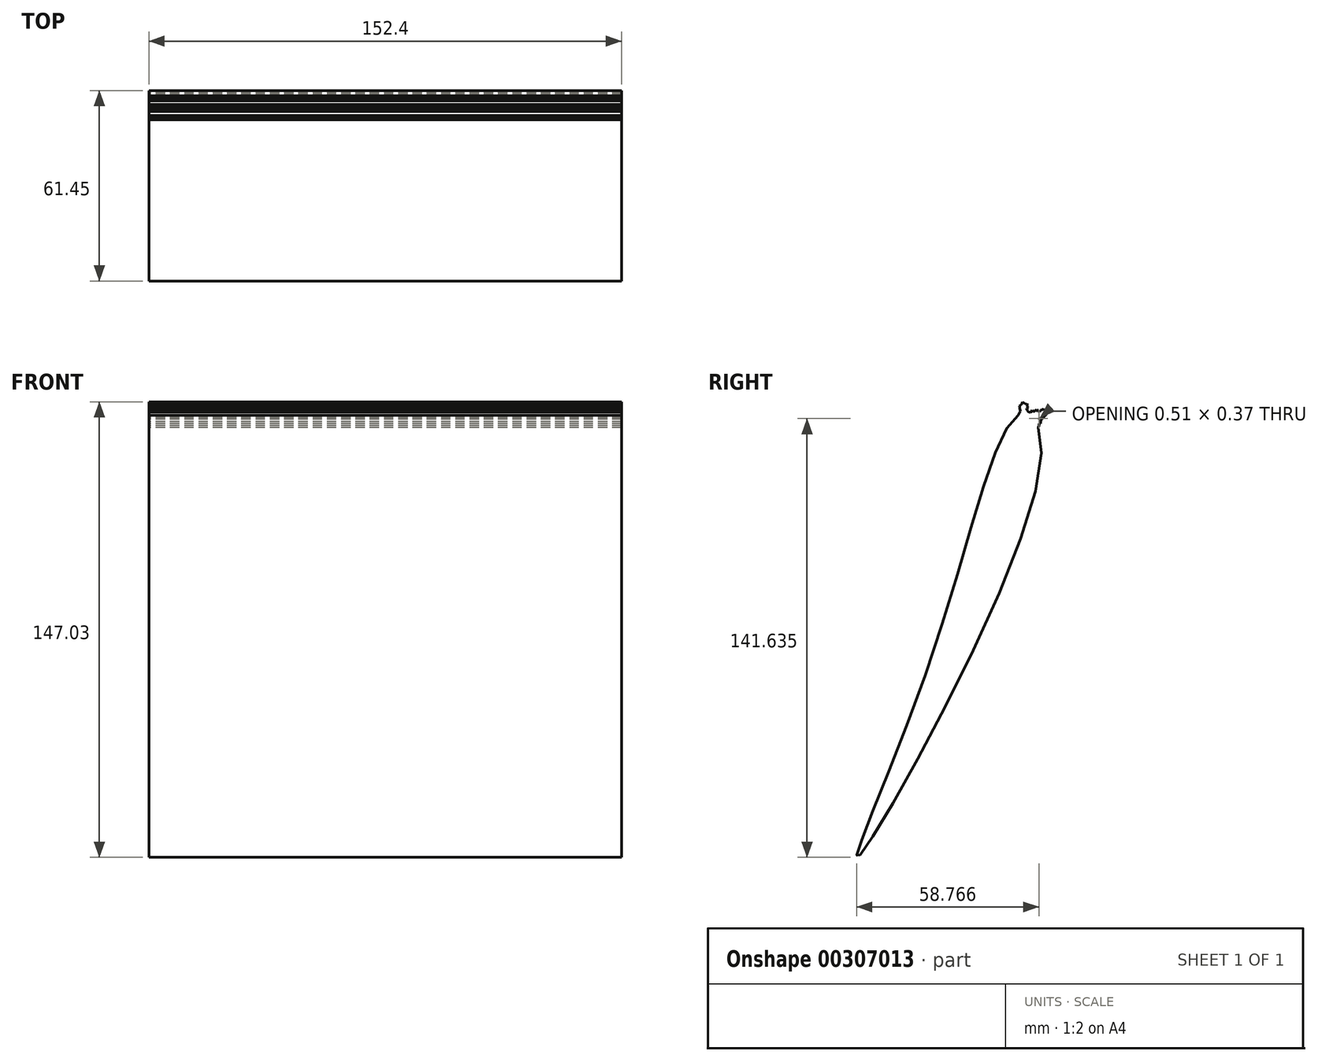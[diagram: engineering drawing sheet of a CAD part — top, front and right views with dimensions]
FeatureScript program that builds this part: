
annotation { "Feature Type Name" : "Feature", "Feature Type Description" : "" }
export const myFeature = defineFeature(function(context is Context, id is Id, definition is map)
    precondition{}
    {
        {
            var Q0;
            Q0=qCreatedBy(makeId("Right.planeOp"),FACE);
            var sketch = newSketch(context, id + "F0", { "sketchPlane" : qUnion([Q0])});
            skFitSpline(sketch, "E0", {"points": [v(49.89, 66.18) * mm, v(56.5, 49.9) * mm, v(-2.03, -76.46) * mm, v(21.12, -12.85) * mm, v(49.89, 66.18) * mm]});
            skLineSegment(sketch, "E1", {"start": v(53.87, 65.13) * mm, "end": v(56.93, 67.06) * mm});
            skLineSegment(sketch, "E2", {"start": v(56.93, 67.06) * mm, "end": v(57.7, 66.01) * mm});
            skLineSegment(sketch, "E3", {"start": v(57.7, 66.01) * mm, "end": v(54.8, 63.9) * mm});
            skLineSegment(sketch, "E4", {"start": v(54.8, 63.9) * mm, "end": v(53.87, 65.13) * mm});
            skLineSegment(sketch, "E5", {"start": v(56.93, 67.06) * mm, "end": v(57.7, 67.62) * mm});
            skPoint(sketch, "E5.endSnap0", {"position": v(57.31, 66.54) * mm});
            skLineSegment(sketch, "E6", {"start": v(57.7, 67.62) * mm, "end": v(58.4, 66.53) * mm});
            skLineSegment(sketch, "E7", {"start": v(58.4, 66.53) * mm, "end": v(57.7, 66.01) * mm});
            skLineSegment(sketch, "E8", {"start": v(51.68, 66.38) * mm, "end": v(51.55, 69.02) * mm});
            skLineSegment(sketch, "E9", {"start": v(51.55, 69.02) * mm, "end": v(50.25, 68.95) * mm});
            skLineSegment(sketch, "E10", {"start": v(50.25, 68.95) * mm, "end": v(50.38, 66.34) * mm});
            skLineSegment(sketch, "E11", {"start": v(50.38, 66.34) * mm, "end": v(51.68, 66.38) * mm});
            skLineSegment(sketch, "E12", {"start": v(55.24, 63.24) * mm, "end": v(55.73, 64.59) * mm});
            skLineSegment(sketch, "E13", {"start": v(55.73, 64.59) * mm, "end": v(56.24, 64.96) * mm});
            skLineSegment(sketch, "E14", {"start": v(56.24, 64.96) * mm, "end": v(56.15, 64.71) * mm});
            skPoint(sketch, "E14.endSnap0", {"position": v(55.99, 64.77) * mm});
            skLineSegment(sketch, "E15", {"start": v(56.15, 64.71) * mm, "end": v(55.73, 64.59) * mm});
            skLineSegment(sketch, "E16", {"start": v(55.48, 63.92) * mm, "end": v(56.31, 64.52) * mm});
            skLineSegment(sketch, "E17", {"start": v(56.31, 64.52) * mm, "end": v(56.56, 65.19) * mm});
            skLineSegment(sketch, "E18", {"start": v(56.56, 65.19) * mm, "end": v(56.89, 64.73) * mm});
            skLineSegment(sketch, "E19", {"start": v(56.89, 64.73) * mm, "end": v(56.31, 64.52) * mm});
            skLineSegment(sketch, "E20", {"start": v(57.3, 65.72) * mm, "end": v(58.09, 65.43) * mm});
            skLineSegment(sketch, "E21", {"start": v(58.09, 65.43) * mm, "end": v(57.7, 66.01) * mm});
            skLineSegment(sketch, "E22", {"start": v(58.4, 66.53) * mm, "end": v(58.23, 65.82) * mm});
            skLineSegment(sketch, "E23", {"start": v(58.23, 65.82) * mm, "end": v(57.4, 65.22) * mm});
            skLineSegment(sketch, "E24", {"start": v(57.4, 65.22) * mm, "end": v(56.56, 65.19) * mm});
            skLineSegment(sketch, "E25", {"start": v(57.4, 65.22) * mm, "end": v(57.3, 64.92) * mm});
            skLineSegment(sketch, "E26", {"start": v(57.3, 64.92) * mm, "end": v(56.89, 64.73) * mm});
            skLineSegment(sketch, "E27", {"start": v(58.23, 65.82) * mm, "end": v(57.7, 66.01) * mm});
            skLineSegment(sketch, "E28", {"start": v(56.89, 64.73) * mm, "end": v(56.55, 63.81) * mm});
            skLineSegment(sketch, "E29", {"start": v(56.55, 63.81) * mm, "end": v(55.48, 63.92) * mm});
            skLineSegment(sketch, "E30", {"start": v(58.4, 66.53) * mm, "end": v(58.67, 67.27) * mm});
            skLineSegment(sketch, "E31", {"start": v(58.67, 67.27) * mm, "end": v(58.16, 66.9) * mm});
            skLineSegment(sketch, "E32", {"start": v(58.16, 66.9) * mm, "end": v(58.67, 67.27) * mm});
            skLineSegment(sketch, "E33", {"start": v(58.67, 67.27) * mm, "end": v(57.7, 67.62) * mm});
            skLineSegment(sketch, "E34", {"start": v(57.7, 67.62) * mm, "end": v(56.94, 67.9) * mm});
            skLineSegment(sketch, "E35", {"start": v(56.94, 67.9) * mm, "end": v(56.66, 67.16) * mm});
            skLineSegment(sketch, "E36", {"start": v(56.66, 67.16) * mm, "end": v(55.66, 67.14) * mm});
            skLineSegment(sketch, "E37", {"start": v(55.66, 67.14) * mm, "end": v(55.28, 67.66) * mm});
            skLineSegment(sketch, "E38", {"start": v(55.28, 67.66) * mm, "end": v(54.89, 66.6) * mm});
            skLineSegment(sketch, "E39", {"start": v(54.89, 66.6) * mm, "end": v(54.74, 66.19) * mm});
            skLineSegment(sketch, "E40", {"start": v(54.74, 66.19) * mm, "end": v(54, 66.27) * mm});
            skLineSegment(sketch, "E41", {"start": v(54, 66.27) * mm, "end": v(53.7, 65.43) * mm});
            skLineSegment(sketch, "E42", {"start": v(53.7, 65.43) * mm, "end": v(53.87, 65.13) * mm});
            skLineSegment(sketch, "E43", {"start": v(55.28, 67.66) * mm, "end": v(54.17, 66.86) * mm});
            skLineSegment(sketch, "E44", {"start": v(54.17, 66.86) * mm, "end": v(53.74, 67.45) * mm});
            skLineSegment(sketch, "E45", {"start": v(53.74, 67.45) * mm, "end": v(53.22, 66.74) * mm});
            skLineSegment(sketch, "E46", {"start": v(53.22, 66.74) * mm, "end": v(52.55, 66.99) * mm});
            skLineSegment(sketch, "E47", {"start": v(52.55, 66.99) * mm, "end": v(51.9, 66.51) * mm});
            skLineSegment(sketch, "E48", {"start": v(52.55, 66.99) * mm, "end": v(52.09, 67.62) * mm});
            skLineSegment(sketch, "E49", {"start": v(52.09, 67.62) * mm, "end": v(51.67, 67.3) * mm});
            skLineSegment(sketch, "E50", {"start": v(51.67, 67.3) * mm, "end": v(51.96, 68.1) * mm});
            skLineSegment(sketch, "E51", {"start": v(51.96, 68.1) * mm, "end": v(51.58, 68.62) * mm});
            skLineSegment(sketch, "E52", {"start": v(51.58, 68.62) * mm, "end": v(51.55, 69.02) * mm});
            skLineSegment(sketch, "E53", {"start": v(51.96, 68.1) * mm, "end": v(52.2, 68.78) * mm});
            skLineSegment(sketch, "E54", {"start": v(52.2, 68.78) * mm, "end": v(51.58, 68.62) * mm});
            skLineSegment(sketch, "E55", {"start": v(52.2, 68.78) * mm, "end": v(52.59, 68.26) * mm});
            skLineSegment(sketch, "E56", {"start": v(52.59, 68.26) * mm, "end": v(51.96, 68.1) * mm});
            skLineSegment(sketch, "E57", {"start": v(52.2, 68.78) * mm, "end": v(52.16, 69.64) * mm});
            skLineSegment(sketch, "E58", {"start": v(52.16, 69.64) * mm, "end": v(51.55, 69.02) * mm});
            skLineSegment(sketch, "E59", {"start": v(51.55, 69.02) * mm, "end": v(51.13, 69.6) * mm});
            skPoint(sketch, "E59.endSnap0", {"position": v(50.9, 68.99) * mm});
            skLineSegment(sketch, "E60", {"start": v(51.13, 69.6) * mm, "end": v(50.25, 68.95) * mm});
            skLineSegment(sketch, "E61", {"start": v(50.25, 68.95) * mm, "end": v(50.7, 70.17) * mm});
            skLineSegment(sketch, "E62", {"start": v(50.7, 70.17) * mm, "end": v(51.86, 69.33) * mm});
            skLineSegment(sketch, "E63", {"start": v(51.86, 69.33) * mm, "end": v(52.16, 69.64) * mm});
            skLineSegment(sketch, "E64", {"start": v(50.43, 69.43) * mm, "end": v(49.72, 68.92) * mm});
            skLineSegment(sketch, "E65", {"start": v(49.72, 68.92) * mm, "end": v(50.34, 67.45) * mm});
            skLineSegment(sketch, "E66", {"start": v(50.34, 67.45) * mm, "end": v(49.8, 68) * mm});
            skLineSegment(sketch, "E67", {"start": v(49.8, 68) * mm, "end": v(49.77, 68.46) * mm});
            skLineSegment(sketch, "E68", {"start": v(49.77, 68.46) * mm, "end": v(49.72, 68.92) * mm});
            skLineSegment(sketch, "E69", {"start": v(50.38, 66.34) * mm, "end": v(49.89, 66.18) * mm});
            skLineSegment(sketch, "E70", {"start": v(49.89, 66.18) * mm, "end": v(49.85, 66.87) * mm});
            skLineSegment(sketch, "E71", {"start": v(49.85, 66.87) * mm, "end": v(50.39, 67.35) * mm});
            skLineSegment(sketch, "E72", {"start": v(50.39, 67.35) * mm, "end": v(49.8, 68) * mm});
            skLineSegment(sketch, "E73", {"start": v(49.8, 68) * mm, "end": v(50.12, 67.1) * mm});
            skLineSegment(sketch, "E74", {"start": v(56.55, 63.81) * mm, "end": v(56.49, 63.12) * mm});
            skLineSegment(sketch, "E75", {"start": v(56.49, 63.12) * mm, "end": v(55.96, 63.1) * mm});
            skLineSegment(sketch, "E76", {"start": v(55.96, 63.1) * mm, "end": v(55.97, 62.47) * mm});
            skLineSegment(sketch, "E77", {"start": v(55.97, 62.47) * mm, "end": v(55.74, 61.85) * mm});
            skLineSegment(sketch, "E78", {"start": v(55.74, 61.85) * mm, "end": v(55.24, 63.24) * mm});
            skLineSegment(sketch, "E79", {"start": v(49.85, 66.87) * mm, "end": v(49.24, 65.86) * mm});
            skLineSegment(sketch, "E80", {"start": v(49.24, 65.86) * mm, "end": v(49.89, 66.18) * mm});
            skLineSegment(sketch, "E81", {"start": v(51.96, 68.1) * mm, "end": v(52.09, 67.62) * mm});
            skLineSegment(sketch, "E82.0", {"start": v(49.85, 66.87) * mm, "end": v(56.31, 64.52) * mm, "construction": true});
            skLineSegment(sketch, "E83.0", {"start": v(49.77, 68.46) * mm, "end": v(58.09, 65.43) * mm, "construction": true});
            skLineSegment(sketch, "E84.0", {"start": v(49.8, 68) * mm, "end": v(52.55, 66.99) * mm, "construction": true});
            skLineSegment(sketch, "E85.0", {"start": v(50.34, 67.45) * mm, "end": v(57.3, 64.92) * mm, "construction": true});
            skLineSegment(sketch, "E86.0", {"start": v(49.72, 68.92) * mm, "end": v(58.23, 65.82) * mm, "construction": true});
            skLineSegment(sketch, "E87.0", {"start": v(50.7, 70.17) * mm, "end": v(58.67, 67.27) * mm, "construction": true});
            skLineSegment(sketch, "E88.0", {"start": v(50.43, 69.43) * mm, "end": v(58.4, 66.53) * mm, "construction": true});
            skLineSegment(sketch, "E89.0", {"start": v(51.58, 68.62) * mm, "end": v(57.31, 66.54) * mm, "construction": true});
            skLineSegment(sketch, "E90.0", {"start": v(55.99, 64.77) * mm, "end": v(56.15, 64.71) * mm, "construction": true});
            skLineSegment(sketch, "E91.0", {"start": v(54.17, 66.86) * mm, "end": v(54.89, 66.6) * mm, "construction": true});
            skLineSegment(sketch, "E92.0", {"start": v(54.74, 66.19) * mm, "end": v(57.4, 65.22) * mm, "construction": true});
            skLineSegment(sketch, "E93.0", {"start": v(50.34, 67.45) * mm, "end": v(51.13, 69.6) * mm, "construction": true});
            skLineSegment(sketch, "E94.0", {"start": v(57.4, 65.22) * mm, "end": v(57.7, 66.01) * mm, "construction": true});
            skLineSegment(sketch, "E95.0", {"start": v(50.25, 68.95) * mm, "end": v(50.43, 69.43) * mm, "construction": true});
            skLineSegment(sketch, "E96.0", {"start": v(57.31, 66.54) * mm, "end": v(57.7, 67.62) * mm, "construction": true});
            skLineSegment(sketch, "E97.0", {"start": v(55.48, 63.92) * mm, "end": v(56.94, 67.9) * mm, "construction": true});
            skLineSegment(sketch, "E98.0", {"start": v(58.09, 65.43) * mm, "end": v(58.23, 65.82) * mm, "construction": true});
            skSolve(sketch);
        }
        {
            var Q0;
            Q0=qSketchRegion(id+"F0",true);
            var Q1;
            Q1=makeQuery(id+"F0.imprint","IMPRINT",FACE,{"disambiguationData":[TD([[makeQuery(id+"F0.imprint","IMPRINT",EDGE,{"derivedFrom":sQuery(id+"F0.wireOp",EDGE,"E1")}),1.0]])]});
            var Q2;
            {var subQ3=sQuery(id+"F0.wireOp",EDGE,"E1");Q2=makeQuery(id+"F0.imprint","IMPRINT",FACE,{"disambiguationData":[TD([[makeQuery(id+"F0.imprint","IMPRINT",EDGE,{"derivedFrom":subQ3}),-1.0]])]});}
            var Q3;
            {var subQ0=sQuery(id+"F0.wireOp",EDGE,"E29");Q3=makeQuery(id+"F0.imprint","IMPRINT",FACE,{"disambiguationData":[TD([[makeQuery(id+"F0.imprint","IMPRINT",EDGE,{"derivedFrom":subQ0}),1.0]])]});}
            var Q4;
            {var subQ0=sQuery(id+"F0.wireOp",EDGE,"E78");var subQ1=sQuery(id+"F0.wireOp",EDGE,"E12");var subQ2=makeQuery(id+"F0.imprint","INTERSECT",VERTEX,{"derivedFrom":[subQ1,subQ0]});Q4=makeQuery(id+"F0.imprint","IMPRINT",FACE,{"disambiguationData":[TD([[makeQuery(id+"F0.imprint","IMPRINT",EDGE,{"disambiguationData":[TD([[subQ2,1.0]])],"derivedFrom":subQ0}),1.0]])]});}
            var Q5;
            {var subQ2=sQuery(id+"F0.wireOp",EDGE,"E8");Q5=makeQuery(id+"F0.imprint","IMPRINT",FACE,{"disambiguationData":[TD([[makeQuery(id+"F0.imprint","IMPRINT",EDGE,{"derivedFrom":subQ2}),-1.0]])]});}
            var Q6;
            {var subQ0=sQuery(id+"F0.wireOp",EDGE,"E11");Q6=makeQuery(id+"F0.imprint","IMPRINT",FACE,{"disambiguationData":[TD([[makeQuery(id+"F0.imprint","IMPRINT",EDGE,{"derivedFrom":subQ0}),1.0]])]});}
            var Q7;
            {var subQ0=sQuery(id+"F0.wireOp",EDGE,"E4");Q7=makeQuery(id+"F0.imprint","IMPRINT",FACE,{"disambiguationData":[TD([[makeQuery(id+"F0.imprint","IMPRINT",EDGE,{"derivedFrom":subQ0}),-1.0]])]});}
            var Q8;
            {var subQ0=sQuery(id+"F0.wireOp",EDGE,"E78");var subQ1=sQuery(id+"F0.wireOp",EDGE,"E0");var subQ3=makeQuery(id+"F0.imprint","INTERSECT",VERTEX,{"derivedFrom":[subQ1,subQ0]});Q8=makeQuery(id+"F0.imprint","IMPRINT",FACE,{"disambiguationData":[TD([[makeQuery(id+"F0.imprint","IMPRINT",EDGE,{"disambiguationData":[TD([[subQ3,-1.0]])],"derivedFrom":subQ1}),-1.0]])]});}
            var Q9;
            {var subQ6=sQuery(id+"F0.wireOp",EDGE,"E8");Q9=makeQuery(id+"F0.imprint","IMPRINT",FACE,{"disambiguationData":[TD([[makeQuery(id+"F0.imprint","IMPRINT",EDGE,{"derivedFrom":subQ6}),1.0]])]});}
            var Q10;
            Q10=makeQuery(id+"F0.imprint","IMPRINT",FACE,{"disambiguationData":[TD([[makeQuery(id+"F0.imprint","IMPRINT",EDGE,{"derivedFrom":sQuery(id+"F0.wireOp",EDGE,"E58")}),-1.0]])]});
            var Q11;
            {var subQ0=sQuery(id+"F0.wireOp",EDGE,"E69");Q11=makeQuery(id+"F0.imprint","IMPRINT",FACE,{"disambiguationData":[TD([[makeQuery(id+"F0.imprint","IMPRINT",EDGE,{"derivedFrom":subQ0}),-1.0]])]});}
            var Q12;
            {var subQ1=sQuery(id+"F0.wireOp",EDGE,"E70");Q12=makeQuery(id+"F0.imprint","IMPRINT",FACE,{"disambiguationData":[TD([[makeQuery(id+"F0.imprint","IMPRINT",EDGE,{"derivedFrom":subQ1}),1.0]])]});}
            var Q13;
            {var subQ0=sQuery(id+"F0.wireOp",EDGE,"E80");Q13=makeQuery(id+"F0.imprint","IMPRINT",FACE,{"disambiguationData":[TD([[makeQuery(id+"F0.imprint","IMPRINT",EDGE,{"derivedFrom":subQ0}),1.0]])]});}
            var Q14;
            {var subQ5=sQuery(id+"F0.wireOp",EDGE,"E64");Q14=makeQuery(id+"F0.imprint","IMPRINT",FACE,{"disambiguationData":[TD([[makeQuery(id+"F0.imprint","IMPRINT",EDGE,{"derivedFrom":subQ5}),1.0]])]});}
            var Q15;
            {var subQ1=sQuery(id+"F0.wireOp",EDGE,"E70");Q15=makeQuery(id+"F0.imprint","IMPRINT",FACE,{"disambiguationData":[TD([[makeQuery(id+"F0.imprint","IMPRINT",EDGE,{"derivedFrom":subQ1}),-1.0]])]});}
            var Q16;
            {var subQ0=sQuery(id+"F0.wireOp",EDGE,"E67");Q16=makeQuery(id+"F0.imprint","IMPRINT",FACE,{"disambiguationData":[TD([[makeQuery(id+"F0.imprint","IMPRINT",EDGE,{"derivedFrom":subQ0}),-1.0]])]});}
            var Q17;
            {var subQ0=sQuery(id+"F0.wireOp",EDGE,"E72");var subQ1=sQuery(id+"F0.wireOp",EDGE,"E10");var subQ2=makeQuery(id+"F0.imprint","INTERSECT",VERTEX,{"derivedFrom":[subQ1,subQ0]});Q17=makeQuery(id+"F0.imprint","IMPRINT",FACE,{"disambiguationData":[TD([[makeQuery(id+"F0.imprint","IMPRINT",EDGE,{"disambiguationData":[TD([[subQ2,-1.0]])],"derivedFrom":subQ1}),1.0]])]});}
            var Q18;
            Q18=makeQuery(id+"F0.imprint","IMPRINT",FACE,{"disambiguationData":[TD([[makeQuery(id+"F0.imprint","IMPRINT",EDGE,{"derivedFrom":sQuery(id+"F0.wireOp",EDGE,"E9")}),-1.0]])]});
            var Q19;
            Q19=makeQuery(id+"F0.imprint","IMPRINT",FACE,{"disambiguationData":[TD([[makeQuery(id+"F0.imprint","IMPRINT",EDGE,{"derivedFrom":sQuery(id+"F0.wireOp",EDGE,"E17")}),-1.0]])]});
            var Q20;
            {var subQ0=sQuery(id+"F0.wireOp",EDGE,"E65");var subQ1=sQuery(id+"F0.wireOp",EDGE,"E10");var subQ2=makeQuery(id+"F0.imprint","INTERSECT",VERTEX,{"derivedFrom":[subQ1,subQ0]});Q20=makeQuery(id+"F0.imprint","IMPRINT",FACE,{"disambiguationData":[TD([[makeQuery(id+"F0.imprint","IMPRINT",EDGE,{"disambiguationData":[TD([[subQ2,-1.0]])],"derivedFrom":subQ1}),1.0]])]});}
            var Q21;
            Q21=makeQuery(id+"F0.imprint","IMPRINT",FACE,{"disambiguationData":[TD([[makeQuery(id+"F0.imprint","IMPRINT",EDGE,{"derivedFrom":sQuery(id+"F0.wireOp",EDGE,"E18")}),1.0]])]});
            var Q22;
            Q22=makeQuery(id+"F0.imprint","IMPRINT",FACE,{"disambiguationData":[TD([[makeQuery(id+"F0.imprint","IMPRINT",EDGE,{"derivedFrom":sQuery(id+"F0.wireOp",EDGE,"E49")}),-1.0]])]});
            var Q23;
            {var subQ2=sQuery(id+"F0.wireOp",EDGE,"E32");Q23=makeQuery(id+"F0.imprint","IMPRINT",FACE,{"disambiguationData":[TD([[makeQuery(id+"F0.imprint","IMPRINT",EDGE,{"derivedFrom":subQ2}),1.0]])]});}
            var Q24;
            {var subQ0=sQuery(id+"F0.wireOp",EDGE,"E66");var subQ1=sQuery(id+"F0.wireOp",EDGE,"E10");var subQ2=makeQuery(id+"F0.imprint","INTERSECT",VERTEX,{"derivedFrom":[subQ1,subQ0]});Q24=makeQuery(id+"F0.imprint","IMPRINT",FACE,{"disambiguationData":[TD([[makeQuery(id+"F0.imprint","IMPRINT",EDGE,{"disambiguationData":[TD([[subQ2,-1.0]])],"derivedFrom":subQ1}),-1.0]])]});}
            var Q25;
            Q25=makeQuery(id+"F0.imprint","IMPRINT",FACE,{"disambiguationData":[TD([[makeQuery(id+"F0.imprint","IMPRINT",EDGE,{"derivedFrom":sQuery(id+"F0.wireOp",EDGE,"E2")}),1.0]])]});
            var Q26;
            {var subQ5=sQuery(id+"F0.wireOp",EDGE,"E73");Q26=makeQuery(id+"F0.imprint","IMPRINT",FACE,{"disambiguationData":[TD([[makeQuery(id+"F0.imprint","IMPRINT",EDGE,{"derivedFrom":subQ5}),1.0]])]});}
            var Q27;
            {var subQ1=sQuery(id+"F0.wireOp",EDGE,"E14");Q27=makeQuery(id+"F0.imprint","IMPRINT",FACE,{"disambiguationData":[TD([[makeQuery(id+"F0.imprint","IMPRINT",EDGE,{"derivedFrom":subQ1}),1.0]])]});}
            var Q28;
            Q28=makeQuery(id+"F0.imprint","IMPRINT",FACE,{"disambiguationData":[TD([[makeQuery(id+"F0.imprint","IMPRINT",EDGE,{"derivedFrom":sQuery(id+"F0.wireOp",EDGE,"E16")}),-1.0]])]});
            var Q29;
            {var subQ0=sQuery(id+"F0.wireOp",EDGE,"E24");Q29=makeQuery(id+"F0.imprint","IMPRINT",FACE,{"disambiguationData":[TD([[makeQuery(id+"F0.imprint","IMPRINT",EDGE,{"derivedFrom":subQ0}),-1.0]])]});}
            var Q30;
            Q30=makeQuery(id+"F0.imprint","IMPRINT",FACE,{"disambiguationData":[TD([[makeQuery(id+"F0.imprint","IMPRINT",EDGE,{"derivedFrom":sQuery(id+"F0.wireOp",EDGE,"E13")}),-1.0]])]});
            var Q31;
            {var subQ0=sQuery(id+"F0.wireOp",EDGE,"E21");var subQ1=sQuery(id+"F0.wireOp",EDGE,"E20");var subQ2=makeQuery(id+"F0.imprint","INTERSECT",VERTEX,{"derivedFrom":[subQ1,subQ0]});Q31=makeQuery(id+"F0.imprint","IMPRINT",FACE,{"disambiguationData":[TD([[makeQuery(id+"F0.imprint","IMPRINT",EDGE,{"disambiguationData":[TD([[subQ2,1.0]])],"derivedFrom":subQ1}),1.0]])]});}
            var Q32;
            Q32=makeQuery(id+"F0.imprint","IMPRINT",FACE,{"disambiguationData":[TD([[makeQuery(id+"F0.imprint","IMPRINT",EDGE,{"derivedFrom":sQuery(id+"F0.wireOp",EDGE,"E53")}),-1.0]])]});
            var Q33;
            {var subQ0=sQuery(id+"F0.wireOp",EDGE,"E30");Q33=makeQuery(id+"F0.imprint","IMPRINT",FACE,{"disambiguationData":[TD([[makeQuery(id+"F0.imprint","IMPRINT",EDGE,{"derivedFrom":subQ0}),1.0]])]});}
            var Q34;
            Q34=makeQuery(id+"F0.imprint","IMPRINT",FACE,{"disambiguationData":[TD([[makeQuery(id+"F0.imprint","IMPRINT",EDGE,{"derivedFrom":sQuery(id+"F0.wireOp",EDGE,"E7")}),1.0]])]});
            var Q35;
            Q35=makeQuery(id+"F0.imprint","IMPRINT",FACE,{"disambiguationData":[TD([[makeQuery(id+"F0.imprint","IMPRINT",EDGE,{"derivedFrom":sQuery(id+"F0.wireOp",EDGE,"E51")}),-1.0]])]});
            var Q36;
            Q36=makeQuery(id+"F0.imprint","IMPRINT",FACE,{"disambiguationData":[TD([[makeQuery(id+"F0.imprint","IMPRINT",EDGE,{"derivedFrom":sQuery(id+"F0.wireOp",EDGE,"E52")}),-1.0]])]});
            var Q37;
            {var subQ1=sQuery(id+"F0.wireOp",EDGE,"E3");var subQ3=sQuery(id+"F0.wireOp",EDGE,"E20");var subQ4=makeQuery(id+"F0.imprint","INTERSECT",VERTEX,{"derivedFrom":[subQ1,subQ3]});Q37=makeQuery(id+"F0.imprint","IMPRINT",FACE,{"disambiguationData":[TD([[makeQuery(id+"F0.imprint","IMPRINT",EDGE,{"disambiguationData":[TD([[subQ4,-1.0]])],"derivedFrom":subQ3}),1.0]])]});}
            var Q38;
            {var subQ0=sQuery(id+"F0.wireOp",EDGE,"E27");Q38=makeQuery(id+"F0.imprint","IMPRINT",FACE,{"disambiguationData":[TD([[makeQuery(id+"F0.imprint","IMPRINT",EDGE,{"derivedFrom":subQ0}),1.0]])]});}
            var Q39;
            {var subQ4=sQuery(id+"F0.wireOp",EDGE,"E4");Q39=makeQuery(id+"F0.imprint","IMPRINT",FACE,{"disambiguationData":[TD([[makeQuery(id+"F0.imprint","IMPRINT",EDGE,{"derivedFrom":subQ4}),1.0]])]});}
            extrude(context, id + "F1", {"entities" : qUnion([Q0, Q1, Q2, Q3, Q4, Q5, Q6, Q7, Q8, Q9, Q10, Q11, Q12, Q13, Q14, Q15, Q16, Q17, Q18, Q19, Q20, Q21, Q22, Q23, Q24, Q25, Q26, Q27, Q28, Q29, Q30, Q31, Q32, Q33, Q34, Q35, Q36, Q37, Q38, Q39]), "depth" : 76.2 * mm, "hasSecondDirection" : true, "secondDirectionOppositeDirection" : true, "secondDirectionDepth" : 76.2 * mm});
        }
    });
